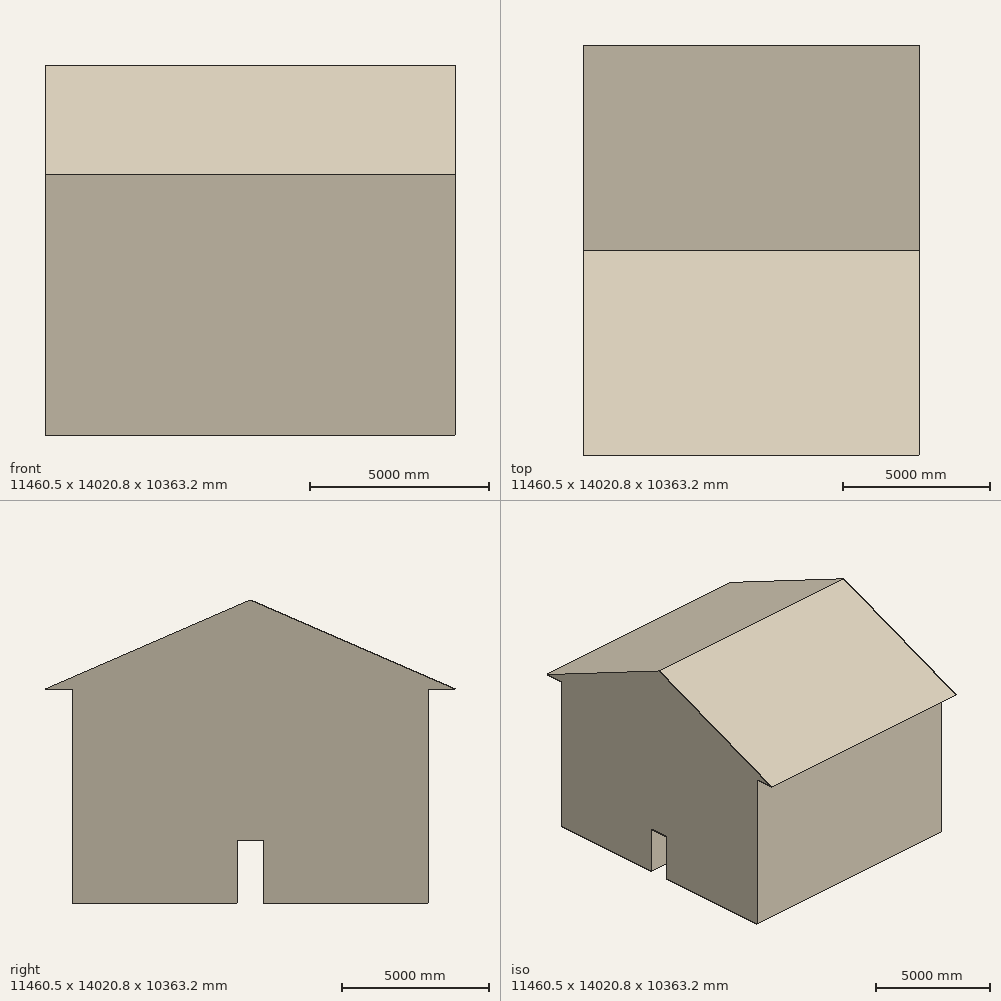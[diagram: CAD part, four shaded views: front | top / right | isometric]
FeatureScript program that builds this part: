
annotation { "Feature Type Name" : "Feature", "Feature Type Description" : "" }
export const myFeature = defineFeature(function(context is Context, id is Id, definition is map)
    precondition{}
    {
        {
            var Q0;
            Q0=qCreatedBy(makeId("Right.planeOp"),FACE);
            var sketch = newSketch(context, id + "F0", { "sketchPlane" : qUnion([Q0])});
            skLineSegment(sketch, "E0", {"start": v(0, 0) * mm, "end": v(-6096, 0) * mm});
            skLineSegment(sketch, "E1", {"start": v(0, 0) * mm, "end": v(6096, 0) * mm});
            skLineSegment(sketch, "E2", {"start": v(-6096, 0) * mm, "end": v(-6096, -7315.2) * mm});
            skLineSegment(sketch, "E3", {"start": v(6096, 0) * mm, "end": v(6096, -7315.2) * mm});
            skLineSegment(sketch, "E4", {"start": v(-6096, -7315.2) * mm, "end": v(6096, -7315.2) * mm});
            skLineSegment(sketch, "E5", {"start": v(-6096, -7315.2) * mm, "end": v(-6096, -7620) * mm});
            skLineSegment(sketch, "E6", {"start": v(-6096, 0) * mm, "end": v(-7010.4, 0) * mm});
            skLineSegment(sketch, "E7", {"start": v(6096, 0) * mm, "end": v(7010.4, 0) * mm});
            skLineSegment(sketch, "E8", {"start": v(0, 3048) * mm, "end": v(7010.4, 0) * mm});
            skLineSegment(sketch, "E9", {"start": v(-7010.4, 0) * mm, "end": v(0, 3048) * mm});
            skLineSegment(sketch, "E10", {"start": v(0, -7315.2) * mm, "end": v(-457.2, -7315.2) * mm});
            skLineSegment(sketch, "E11", {"start": v(-457.2, -7315.2) * mm, "end": v(-457.2, -5181.6) * mm});
            skLineSegment(sketch, "E12", {"start": v(-457.2, -5181.6) * mm, "end": v(457.2, -5181.6) * mm});
            skLineSegment(sketch, "E13", {"start": v(457.2, -5181.6) * mm, "end": v(457.2, -7315.2) * mm});
            skLineSegment(sketch, "E14", {"start": v(0, 3048) * mm, "end": v(0, 2590.8) * mm});
            skLineSegment(sketch, "E15", {"start": v(0, 2590.8) * mm, "end": v(-6096, 0) * mm});
            skLineSegment(sketch, "E16", {"start": v(0, 2590.8) * mm, "end": v(6096, 0) * mm});
            skLineSegment(sketch, "E17.bottom", {"start": v(-5319.93, -811.45) * mm, "end": v(-2891.27, -811.45) * mm});
            skLineSegment(sketch, "E17.top", {"start": v(-5319.93, -2517.3) * mm, "end": v(-2891.27, -2517.3) * mm});
            skLineSegment(sketch, "E17.left", {"start": v(-5319.93, -811.45) * mm, "end": v(-5319.93, -2517.3) * mm});
            skLineSegment(sketch, "E17.right", {"start": v(-2891.27, -811.45) * mm, "end": v(-2891.27, -2517.3) * mm});
            skLineSegment(sketch, "E18.bottom", {"start": v(2110.62, -811.45) * mm, "end": v(4712.76, -811.45) * mm});
            skLineSegment(sketch, "E18.top", {"start": v(2110.62, -2517.3) * mm, "end": v(4712.76, -2517.3) * mm});
            skLineSegment(sketch, "E18.left", {"start": v(2110.62, -811.45) * mm, "end": v(2110.62, -2517.3) * mm});
            skLineSegment(sketch, "E18.right", {"start": v(4712.76, -811.45) * mm, "end": v(4712.76, -2517.3) * mm});
            skLineSegment(sketch, "E19.bottom", {"start": v(2110.62, -4396.62) * mm, "end": v(4799.5, -4396.62) * mm});
            skLineSegment(sketch, "E19.top", {"start": v(2110.62, -6189.2) * mm, "end": v(4799.5, -6189.2) * mm});
            skLineSegment(sketch, "E19.left", {"start": v(2110.62, -4396.62) * mm, "end": v(2110.62, -6189.2) * mm});
            skLineSegment(sketch, "E19.right", {"start": v(4799.5, -4396.62) * mm, "end": v(4799.5, -6189.2) * mm});
            skLineSegment(sketch, "E20.bottom", {"start": v(-2891.27, -4396.62) * mm, "end": v(-5406.67, -4396.62) * mm});
            skLineSegment(sketch, "E20.top", {"start": v(-2891.27, -6391.6) * mm, "end": v(-5406.67, -6391.6) * mm});
            skLineSegment(sketch, "E20.left", {"start": v(-2891.27, -4396.62) * mm, "end": v(-2891.27, -6391.6) * mm});
            skLineSegment(sketch, "E20.right", {"start": v(-5406.67, -4396.62) * mm, "end": v(-5406.67, -6391.6) * mm});
            skSolve(sketch);
        }
        {
            var Q0;
            Q0=makeQuery(id+"F0.imprint","IMPRINT",FACE,{"disambiguationData":[TD([[makeQuery(id+"F0.imprint","IMPRINT",EDGE,{"derivedFrom":sQuery(id+"F0.wireOp",EDGE,"E19.bottom")}),-1.0]])]});
            var Q1;
            Q1=makeQuery(id+"F0.imprint","IMPRINT",FACE,{"disambiguationData":[TD([[makeQuery(id+"F0.imprint","IMPRINT",EDGE,{"derivedFrom":sQuery(id+"F0.wireOp",EDGE,"E6")}),-1.0]])]});
            var Q2;
            Q2=makeQuery(id+"F0.imprint","IMPRINT",FACE,{"disambiguationData":[TD([[makeQuery(id+"F0.imprint","IMPRINT",EDGE,{"derivedFrom":sQuery(id+"F0.wireOp",EDGE,"E20.bottom")}),1.0]])]});
            var Q3;
            Q3=makeQuery(id+"F0.imprint","IMPRINT",FACE,{"disambiguationData":[TD([[makeQuery(id+"F0.imprint","IMPRINT",EDGE,{"derivedFrom":sQuery(id+"F0.wireOp",EDGE,"E7")}),1.0]])]});
            var Q4;
            Q4=makeQuery(id+"F0.imprint","IMPRINT",FACE,{"disambiguationData":[TD([[makeQuery(id+"F0.imprint","IMPRINT",EDGE,{"derivedFrom":sQuery(id+"F0.wireOp",EDGE,"E0")}),-1.0]])]});
            var Q5;
            {var subQ0=sQuery(id+"F0.wireOp",EDGE,"E10");Q5=makeQuery(id+"F0.imprint","IMPRINT",FACE,{"disambiguationData":[TD([[makeQuery(id+"F0.imprint","IMPRINT",EDGE,{"derivedFrom":subQ0}),-1.0]])]});}
            var Q6;
            Q6=makeQuery(id+"F0.imprint","IMPRINT",FACE,{"disambiguationData":[TD([[makeQuery(id+"F0.imprint","IMPRINT",EDGE,{"derivedFrom":sQuery(id+"F0.wireOp",EDGE,"E0")}),1.0]])]});
            var Q7;
            Q7=makeQuery(id+"F0.imprint","IMPRINT",FACE,{"disambiguationData":[TD([[makeQuery(id+"F0.imprint","IMPRINT",EDGE,{"derivedFrom":sQuery(id+"F0.wireOp",EDGE,"E18.bottom")}),-1.0]])]});
            var Q8;
            Q8=makeQuery(id+"F0.imprint","IMPRINT",FACE,{"disambiguationData":[TD([[makeQuery(id+"F0.imprint","IMPRINT",EDGE,{"derivedFrom":sQuery(id+"F0.wireOp",EDGE,"E17.bottom")}),-1.0]])]});
            extrude(context, id + "F1", {"entities" : qUnion([Q0, Q1, Q2, Q3, Q4, Q5, Q6, Q7, Q8]), "depth" : 11460.48 * mm, "offsetDistance" : 30.48 * mm});
        }
    });
